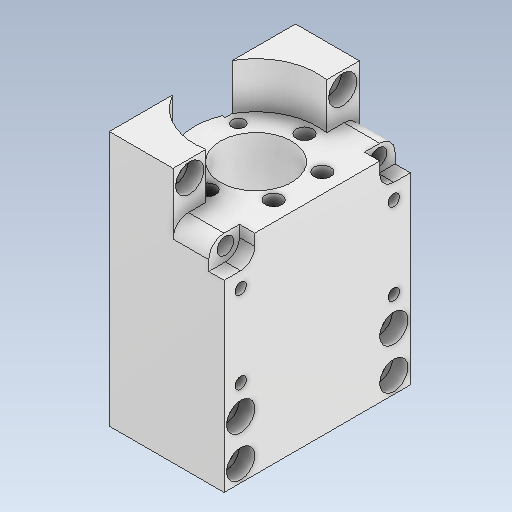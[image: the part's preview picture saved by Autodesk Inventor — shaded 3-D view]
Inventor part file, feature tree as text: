
AUTODESK INVENTOR PART (.ipt)
format: ipt  version: 2020 (Build 240168000, 168)  size: 486,400 bytes
history: native  units: mm
features: extrude x13, sketch x10, other x2, fillet x1, projected_geometry x1
ambient origin geometry x8: Origin, YZ Plane, XZ Plane, XY Plane, X Axis, Y Axis, Z Axis, Center Point
bodies: Body1 (feature_tree)
feature tree (27):
  other  "Bryła1"
  extrude  "Wyciągnięcie proste1"  Depth=73.0mm
  sketch  "Szkic2"
  extrude  "Wyciągnięcie proste2"  Depth=100.0mm
  extrude  "Wyciągnięcie proste4"  Depth=45.0mm TaperAngle=0.0deg
  extrude  "Wyciągnięcie proste5"  Depth=48.0mm
  extrude  "Wyciągnięcie proste6"  Depth=18.0mm TaperAngle=0.0deg
  extrude  "Wyciągnięcie proste7"  Depth=28.0mm
  extrude  "Wyciągnięcie proste8"  Depth=48.0mm
  extrude  "Wyciągnięcie proste9"  Depth=10.0mm TaperAngle=0.0deg
  extrude  "Wyciągnięcie proste10"  Depth=44.0mm TaperAngle=0.0deg
  sketch  "Szkic8"
  extrude  "Wyciągnięcie proste11"  Depth=6.5mm
  other  "Płaszczyzna konstrukcyjna1"
  extrude  "Wyciągnięcie proste12"  Depth=6.5mm
  extrude  "Wyciągnięcie proste13"  Depth=6.5mm
  extrude  "Wyciągnięcie proste14"  Depth=16.0mm
  fillet  "Zaokrąglenie1"  [1 undecoded]
  sketch  "Szkic1"
  sketch  "Szkic3"
  sketch  "Szkic4"
  sketch  "Szkic5"
  sketch  "Szkic6"
  projected_geometry  "Pętla rzutowana1"
  sketch  "Szkic7"
  sketch  "Szkic9"
  sketch  "Szkic10"
note: 1 required parameter value undecoded (feature->parameter linkage not recoverable at this tier; creation-order binding heuristic only, values carry confidence <= 0.55)
